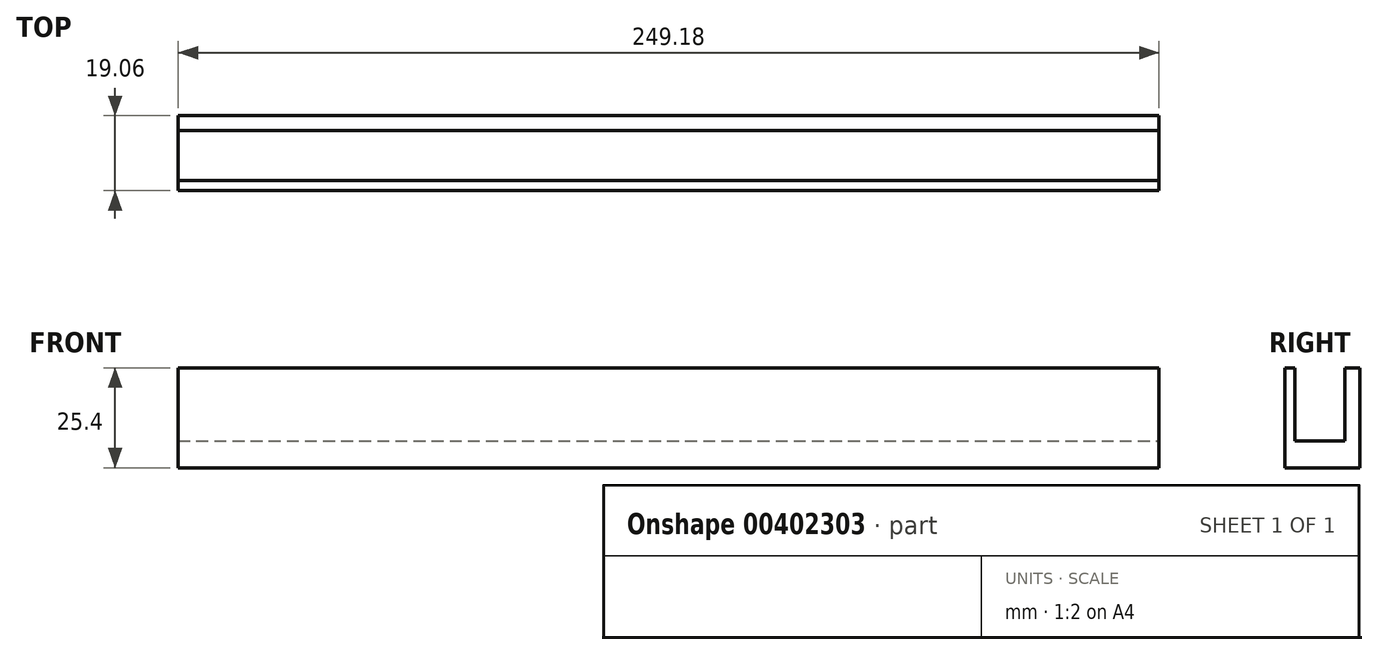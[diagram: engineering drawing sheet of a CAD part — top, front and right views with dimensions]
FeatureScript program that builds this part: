
annotation { "Feature Type Name" : "Feature", "Feature Type Description" : "" }
export const myFeature = defineFeature(function(context is Context, id is Id, definition is map)
    precondition{}
    {
        {
            var Q0;
            Q0=qCreatedBy(makeId("Top.planeOp"),FACE);
            var sketch = newSketch(context, id + "F0", { "sketchPlane" : qUnion([Q0])});
            skLineSegment(sketch, "E0.bottom", {"start": v(-124.59, 9.53) * mm, "end": v(124.59, 9.53) * mm});
            skLineSegment(sketch, "E0.top", {"start": v(-124.59, -9.53) * mm, "end": v(124.59, -9.53) * mm});
            skLineSegment(sketch, "E0.left", {"start": v(-124.59, 9.53) * mm, "end": v(-124.59, -9.53) * mm});
            skLineSegment(sketch, "E0.right", {"start": v(124.59, 9.53) * mm, "end": v(124.59, -9.53) * mm});
            skPoint(sketch, "E0.middle", {"position": v(0, 0) * mm});
            skSolve(sketch);
        }
        {
            var Q0;
            Q0 = qSketchRegion(id + "F0", true);
            extrude(context, id + "F1", {"entities" : qUnion([Q0]), "depth" : 25.4 * mm, "symmetric" : true});
        }
        {
            var Q0;
            Q0=makeQuery(id+"F1.opExtrude","SWEPT_FACE",FACE,{"disambiguationData":[OSD([sQuery(id+"F0.wireOp",EDGE,"E0.right")])]});
            var sketch = newSketch(context, id + "F2", { "sketchPlane" : qUnion([Q0])});
            skLineSegment(sketch, "E1.bottom", {"start": v(-6.98, 12.7) * mm, "end": v(5.72, 12.7) * mm});
            skLineSegment(sketch, "E1.top", {"start": v(-6.98, -5.83) * mm, "end": v(5.72, -5.83) * mm});
            skLineSegment(sketch, "E1.left", {"start": v(-6.98, 12.7) * mm, "end": v(-6.98, -5.83) * mm});
            skLineSegment(sketch, "E1.right", {"start": v(5.72, 12.7) * mm, "end": v(5.72, -5.83) * mm});
            skSolve(sketch);
        }
        {
            var Q0;
            Q0 = qSketchRegion(id + "F2", true);
            extrude(context, id + "F3", {"entities" : qUnion([Q0]), "operationType" : NewBodyOperationType.REMOVE, "endBound" : BoundingType.THROUGH_ALL, "oppositeDirection" : true, "depth" : 25.4 * mm});
        }
    });
